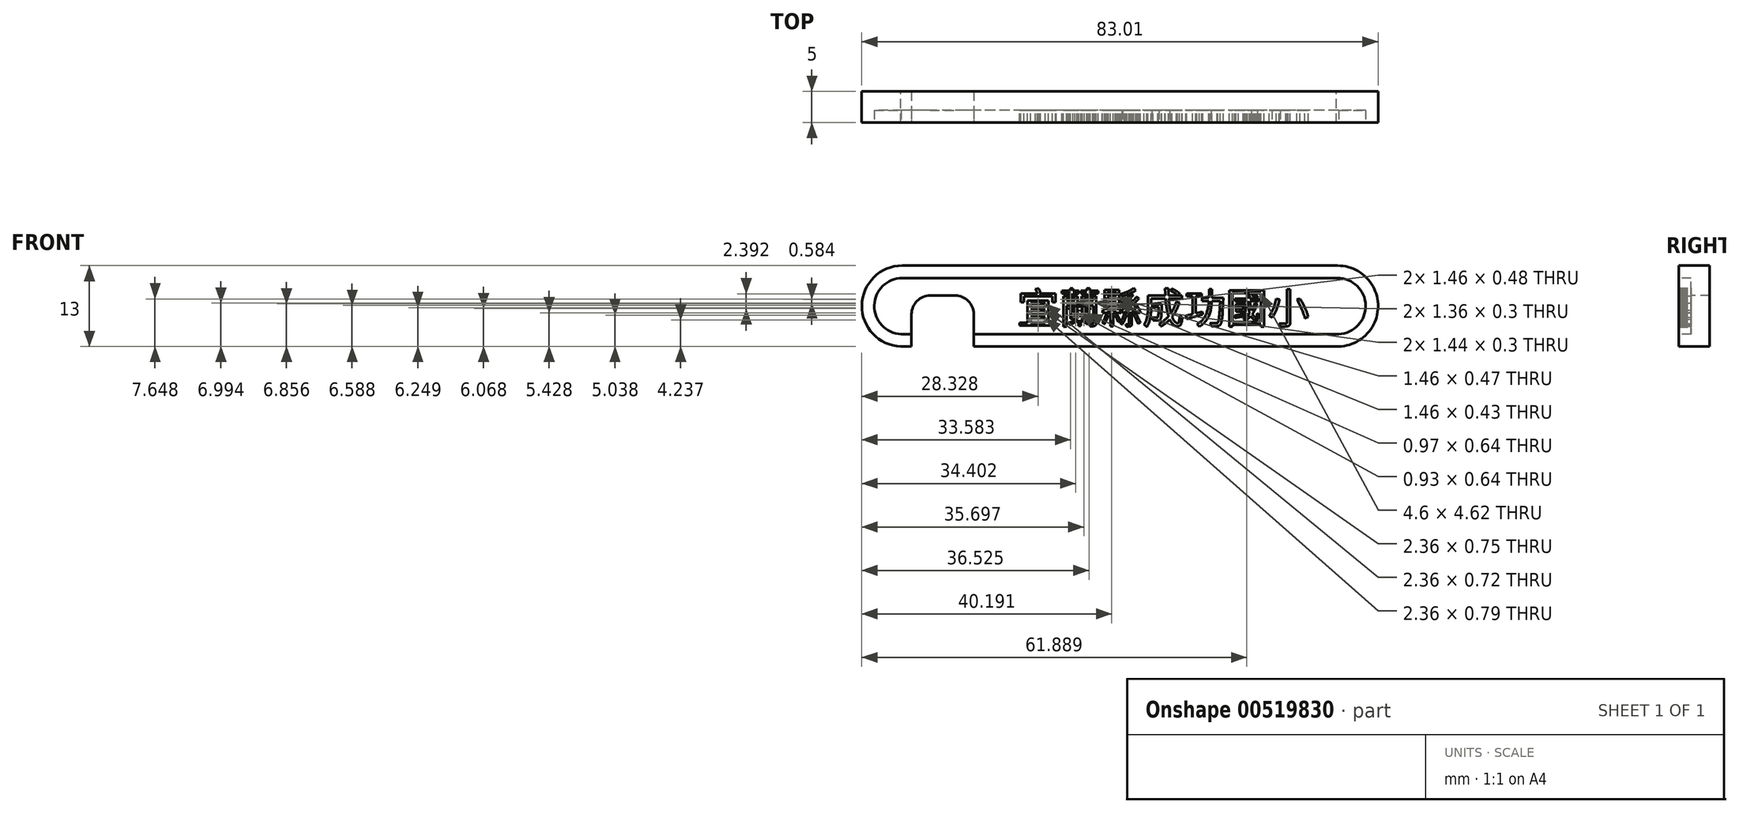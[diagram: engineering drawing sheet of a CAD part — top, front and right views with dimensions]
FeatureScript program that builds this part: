
annotation { "Feature Type Name" : "Feature", "Feature Type Description" : "" }
export const myFeature = defineFeature(function(context is Context, id is Id, definition is map)
    precondition{}
    {
        {
            var Q0;
            Q0=qCreatedBy(makeId("Front.planeOp"),FACE);
            var sketch = newSketch(context, id + "F0", { "sketchPlane" : qUnion([Q0])});
            skLineSegment(sketch, "E0.bottom", {"start": v(34.88, -6.5) * mm, "end": v(-35.12, -6.5) * mm});
            skLineSegment(sketch, "E0.top", {"start": v(35.12, 6.5) * mm, "end": v(-34.88, 6.5) * mm});
            skPoint(sketch, "E0.middle", {"position": v(0, 0) * mm});
            skArc(sketch, "E1", {"start": v(-34.88, 6.5) * mm, "mid": v(-41.39, 0.11) * mm, "end": v(-35.12, -6.5) * mm});
            skArc(sketch, "E2", {"start": v(35.12, 6.5) * mm, "mid": v(41.62, -0.12) * mm, "end": v(34.88, -6.5) * mm});
            skSolve(sketch);
        }
        {
            var Q0;
            Q0 = qSketchRegion(id + "F0", true);
            extrude(context, id + "F1", {"entities" : qUnion([Q0]), "depth" : 5 * mm, "offsetDistance" : 25 * mm});
        }
        {
            var Q0;
            Q0=makeQuery(id+"F1.opExtrude","CAP_FACE",FACE,{"disambiguationData":[OSD([sQuery(id+"F0.wireOp",EDGE,"E0.bottom"),sQuery(id+"F0.wireOp",EDGE,"E0.top"),sQuery(id+"F0.wireOp",EDGE,"E1"),sQuery(id+"F0.wireOp",EDGE,"E2")])],"isStart":false});
            var sketch = newSketch(context, id + "F2", { "sketchPlane" : qUnion([Q0])});
            skLineSegment(sketch, "E3.0", {"start": v(35.12, 4.5) * mm, "end": v(-34.88, 4.5) * mm});
            skArc(sketch, "E3.1", {"start": v(35.12, 4.5) * mm, "mid": v(39.62, 0.1) * mm, "end": v(35.3, -4.5) * mm});
            skLineSegment(sketch, "E3.2", {"start": v(35.3, -4.5) * mm, "end": v(-35.08, -4.5) * mm});
            skArc(sketch, "E3.3", {"start": v(-34.88, 4.5) * mm, "mid": v(-39.39, 0.1) * mm, "end": v(-35.08, -4.5) * mm});
            skSolve(sketch);
        }
        {
            var Q0;
            Q0=makeQuery(id+"F2.imprint","IMPRINT",FACE,{"disambiguationData":[TD([[makeQuery(id+"F2.imprint","IMPRINT",EDGE,{"derivedFrom":sQuery(id+"F2.wireOp",EDGE,"E3.0")}),1.0]])]});
            extrude(context, id + "F3", {"entities" : qUnion([Q0]), "operationType" : NewBodyOperationType.REMOVE, "oppositeDirection" : true, "depth" : 2 * mm, "offsetDistance" : 25 * mm});
        }
        {
            var Q0;
            Q0=makeQuery(id+"F1.opExtrude","CAP_FACE",FACE,{"disambiguationData":[OSD([sQuery(id+"F0.wireOp",EDGE,"E0.bottom"),sQuery(id+"F0.wireOp",EDGE,"E0.top"),sQuery(id+"F0.wireOp",EDGE,"E1"),sQuery(id+"F0.wireOp",EDGE,"E2")])],"isStart":false});
            var sketch = newSketch(context, id + "F4", { "sketchPlane" : qUnion([Q0])});
            skLineSegment(sketch, "E4.bottom", {"start": v(-30.39, 1.7) * mm, "end": v(-26.39, 1.7) * mm});
            skLineSegment(sketch, "E4.top", {"start": v(-33.39, -6.5) * mm, "end": v(-23.39, -6.5) * mm});
            skLineSegment(sketch, "E4.left", {"start": v(-33.39, -1.3) * mm, "end": v(-33.39, -6.5) * mm});
            skLineSegment(sketch, "E4.right", {"start": v(-23.39, -1.3) * mm, "end": v(-23.39, -6.5) * mm});
            skPoint(sketch, "E5.visualSharp", {"position": v(-33.39, 1.7) * mm});
            skArc(sketch, "E5.filletArc", {"start": v(-30.39, 1.7) * mm, "mid": v(-32.5, 0.82) * mm, "end": v(-33.39, -1.3) * mm});
            skPoint(sketch, "E6.visualSharp", {"position": v(-23.39, 1.7) * mm});
            skArc(sketch, "E6.filletArc", {"start": v(-23.39, -1.3) * mm, "mid": v(-24.26, 0.82) * mm, "end": v(-26.39, 1.7) * mm});
            skSolve(sketch);
        }
        {
            var Q0;
            Q0 = qSketchRegion(id + "F4", true);
            extrude(context, id + "F5", {"entities" : qUnion([Q0]), "operationType" : NewBodyOperationType.REMOVE, "endBound" : BoundingType.THROUGH_ALL, "oppositeDirection" : true, "depth" : 25 * mm, "offsetDistance" : 25 * mm});
        }
        {
            var Q0;
            Q0=makeQuery(id+"F3.boolean.opBoolean","COPY",FACE,{"derivedFrom":makeQuery(id+"F3.opExtrude","CAP_FACE",FACE,{"disambiguationData":[OSD([sQuery(id+"F2.wireOp",EDGE,"E3.0"),sQuery(id+"F2.wireOp",EDGE,"E3.1"),sQuery(id+"F2.wireOp",EDGE,"E3.2"),sQuery(id+"F2.wireOp",EDGE,"E3.3")])],"isStart":false})});
            var sketch = newSketch(context, id + "F6", { "sketchPlane" : qUnion([Q0])});
            skText(sketch, "E7", { "text": "宜蘭縣成功國小", "fontName": "NotoSansCJKtc-Regular.otf"});
            const initialGuessF6  = {"E7": [-0.01639, -0.00279, 1, 0, 0.00483]};
            skSetInitialGuess(sketch, initialGuessF6);
            skSolve(sketch);
        }
        {
            var Q0;
            Q0 = qSketchRegion(id + "F6", true);
            extrude(context, id + "F7", {"entities" : qUnion([Q0]), "depth" : 2 * mm, "offsetDistance" : 25 * mm});
        }
        {
            var Q0;
            Q0=makeQuery(id+"F6.imprint","IMPRINT",FACE,{"disambiguationData":[TD([[makeQuery(id+"F6.imprint","IMPRINT",EDGE,{"derivedFrom":sQuery(id+"F6.wireOp",EDGE,"E7.sketch_text.stroke-295")}),1.0]])]});
            extrude(context, id + "F8", {"entities" : qUnion([Q0]), "operationType" : NewBodyOperationType.ADD, "depth" : 2 * mm, "offsetDistance" : 25 * mm});
        }
        {
            var Q0;
            Q0=makeQuery(id+"F6.imprint","IMPRINT",FACE,{"disambiguationData":[TD([[makeQuery(id+"F6.imprint","IMPRINT",EDGE,{"derivedFrom":sQuery(id+"F6.wireOp",EDGE,"E7.sketch_text.stroke-287")}),1.0]])]});
            extrude(context, id + "F9", {"entities" : qUnion([Q0]), "operationType" : NewBodyOperationType.ADD, "depth" : 2 * mm, "offsetDistance" : 25 * mm});
        }
        {
            var Q0;
            Q0=makeQuery(id+"F6.imprint","IMPRINT",FACE,{"disambiguationData":[TD([[makeQuery(id+"F6.imprint","IMPRINT",EDGE,{"derivedFrom":sQuery(id+"F6.wireOp",EDGE,"E7.sketch_text.stroke-283")}),1.0]])]});
            extrude(context, id + "F10", {"entities" : qUnion([Q0]), "operationType" : NewBodyOperationType.ADD, "depth" : 2 * mm, "offsetDistance" : 25 * mm});
        }
        {
            var Q0;
            Q0=makeQuery(id+"F6.imprint","IMPRINT",FACE,{"disambiguationData":[TD([[makeQuery(id+"F6.imprint","IMPRINT",EDGE,{"derivedFrom":sQuery(id+"F6.wireOp",EDGE,"E7.sketch_text.stroke-279")}),1.0]])]});
            extrude(context, id + "F11", {"entities" : qUnion([Q0]), "operationType" : NewBodyOperationType.ADD, "depth" : 2 * mm, "offsetDistance" : 25 * mm});
        }
    });
